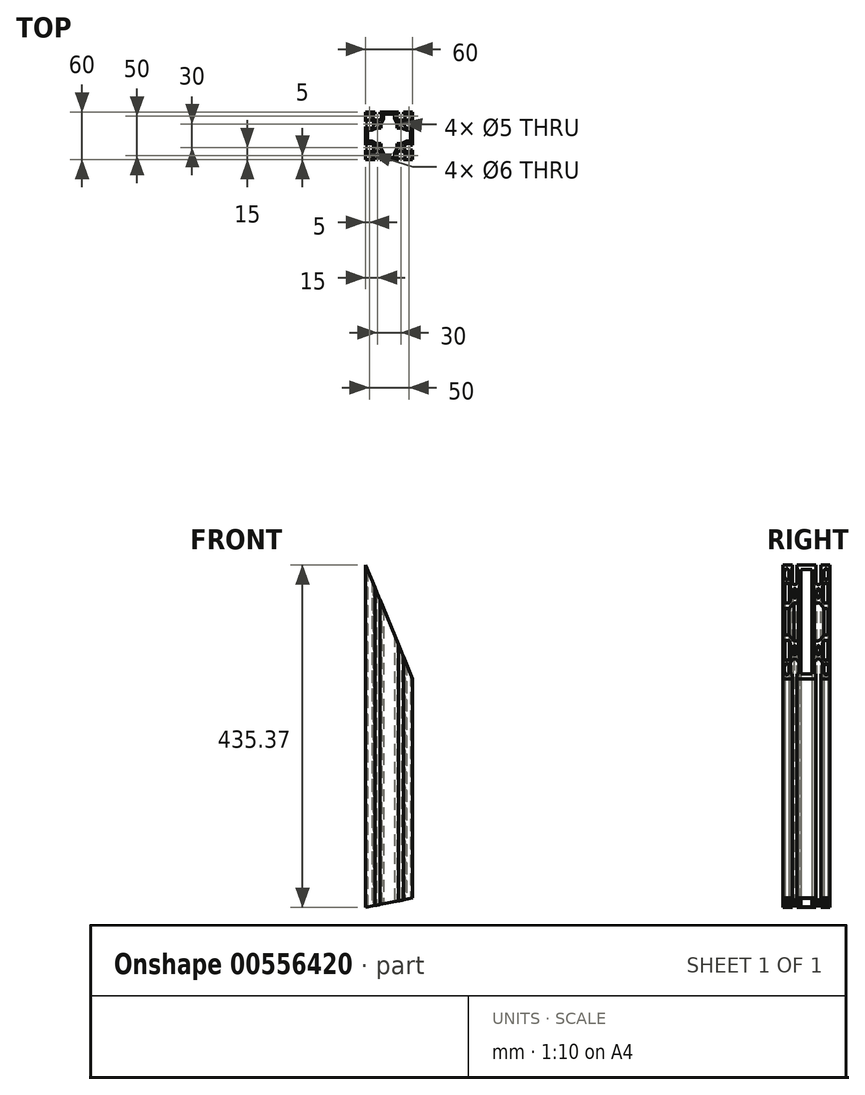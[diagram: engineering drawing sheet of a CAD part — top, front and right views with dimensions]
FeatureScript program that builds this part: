
annotation { "Feature Type Name" : "Feature", "Feature Type Description" : "" }
export const myFeature = defineFeature(function(context is Context, id is Id, definition is map)
    precondition{}
    {
        {
            var Q0;
            Q0=qCreatedBy(makeId("Top.planeOp"),FACE);
            var sketch = newSketch(context, id + "F0", { "sketchPlane" : qUnion([Q0])});
            skLineSegment(sketch, "E0.bottom", {"start": v(30, -30) * mm, "end": v(-30, -30) * mm});
            skLineSegment(sketch, "E0.top", {"start": v(30, 30) * mm, "end": v(-30, 30) * mm});
            skLineSegment(sketch, "E0.left", {"start": v(30, -30) * mm, "end": v(30, 30) * mm});
            skLineSegment(sketch, "E0.right", {"start": v(-30, -30) * mm, "end": v(-30, 30) * mm});
            skPoint(sketch, "E0.middle", {"position": v(0, 0) * mm});
            skLineSegment(sketch, "E1.top", {"start": v(-11.85, 30) * mm, "end": v(-18.15, 30) * mm});
            skLineSegment(sketch, "E1.left", {"start": v(-11.85, 27.5) * mm, "end": v(-11.85, 30) * mm});
            skLineSegment(sketch, "E1.right", {"start": v(-18.15, 27.5) * mm, "end": v(-18.15, 30) * mm});
            skPoint(sketch, "E1.middle", {"position": v(-15, 28.75) * mm});
            skLineSegment(sketch, "E2.bottom", {"start": v(-9.85, 27.5) * mm, "end": v(-11.85, 27.5) * mm});
            skLineSegment(sketch, "E2.left", {"start": v(-9.85, 27.5) * mm, "end": v(-9.85, 21.55) * mm});
            skLineSegment(sketch, "E2.right", {"start": v(-20.15, 27.5) * mm, "end": v(-20.15, 21.55) * mm});
            skPoint(sketch, "E2.middle", {"position": v(-15, 24.52) * mm});
            skArc(sketch, "E3", {"start": v(-20.15, 21.55) * mm, "mid": v(-15, 19.5) * mm, "end": v(-9.85, 21.55) * mm});
            skPoint(sketch, "E4.MirrorP", {"position": v(15, 24.52) * mm});
            skPoint(sketch, "E5.MirrorP", {"position": v(15, 28.75) * mm});
            skLineSegment(sketch, "E6.MirrorCS", {"start": v(11.85, 27.5) * mm, "end": v(11.85, 30) * mm});
            skLineSegment(sketch, "E7.MirrorCS", {"start": v(18.15, 27.5) * mm, "end": v(18.15, 30) * mm});
            skLineSegment(sketch, "E8.MirrorCS", {"start": v(9.85, 27.5) * mm, "end": v(11.85, 27.5) * mm});
            skLineSegment(sketch, "E9.MirrorCS", {"start": v(9.85, 27.5) * mm, "end": v(9.85, 21.55) * mm});
            skArc(sketch, "E10.MirrorCS", {"start": v(20.15, 21.55) * mm, "mid": v(15, 19.5) * mm, "end": v(9.85, 21.55) * mm});
            skLineSegment(sketch, "E11.MirrorCS", {"start": v(20.15, 27.5) * mm, "end": v(20.15, 21.55) * mm});
            skLineSegment(sketch, "E12.MirrorCS", {"start": v(11.85, 30) * mm, "end": v(18.15, 30) * mm});
            skLineSegment(sketch, "E13.1.0", {"start": v(27.5, 20.15) * mm, "end": v(21.55, 20.15) * mm});
            skLineSegment(sketch, "E13.1.1", {"start": v(27.5, 9.85) * mm, "end": v(21.55, 9.85) * mm});
            skArc(sketch, "E13.1.2", {"start": v(21.55, 20.15) * mm, "mid": v(19.5, 15) * mm, "end": v(21.55, 9.85) * mm});
            skLineSegment(sketch, "E13.1.3", {"start": v(27.5, -9.85) * mm, "end": v(21.55, -9.85) * mm});
            skLineSegment(sketch, "E13.1.4", {"start": v(27.5, -20.15) * mm, "end": v(21.55, -20.15) * mm});
            skPoint(sketch, "E13.1.5", {"position": v(28.75, 15) * mm});
            skPoint(sketch, "E13.1.6", {"position": v(28.75, -15) * mm});
            skArc(sketch, "E13.1.7", {"start": v(21.55, -20.15) * mm, "mid": v(19.5, -15) * mm, "end": v(21.55, -9.85) * mm});
            skPoint(sketch, "E13.1.8", {"position": v(24.52, -15) * mm});
            skPoint(sketch, "E13.1.9", {"position": v(24.52, 15) * mm});
            skLineSegment(sketch, "E13.1.10", {"start": v(27.5, 9.85) * mm, "end": v(27.5, 20.15) * mm});
            skLineSegment(sketch, "E13.1.11", {"start": v(27.5, -11.85) * mm, "end": v(27.5, -18.15) * mm});
            skLineSegment(sketch, "E13.1.12", {"start": v(30, 11.85) * mm, "end": v(30, 18.15) * mm});
            skLineSegment(sketch, "E13.1.13", {"start": v(30, -11.85) * mm, "end": v(30, -18.15) * mm});
            skLineSegment(sketch, "E13.1.14", {"start": v(27.5, 18.15) * mm, "end": v(30, 18.15) * mm});
            skLineSegment(sketch, "E13.1.15", {"start": v(27.5, 11.85) * mm, "end": v(30, 11.85) * mm});
            skLineSegment(sketch, "E13.1.16", {"start": v(27.5, 11.85) * mm, "end": v(27.5, 18.15) * mm});
            skLineSegment(sketch, "E13.1.17", {"start": v(27.5, -9.85) * mm, "end": v(27.5, -20.15) * mm});
            skLineSegment(sketch, "E13.1.18", {"start": v(27.5, -18.15) * mm, "end": v(30, -18.15) * mm});
            skLineSegment(sketch, "E13.1.19", {"start": v(27.5, -11.85) * mm, "end": v(30, -11.85) * mm});
            skLineSegment(sketch, "E13.2.0", {"start": v(20.15, -27.5) * mm, "end": v(20.15, -21.55) * mm});
            skLineSegment(sketch, "E13.2.1", {"start": v(9.85, -27.5) * mm, "end": v(9.85, -21.55) * mm});
            skArc(sketch, "E13.2.2", {"start": v(20.15, -21.55) * mm, "mid": v(15, -19.5) * mm, "end": v(9.85, -21.55) * mm});
            skLineSegment(sketch, "E13.2.3", {"start": v(-9.85, -27.5) * mm, "end": v(-9.85, -21.55) * mm});
            skLineSegment(sketch, "E13.2.4", {"start": v(-20.15, -27.5) * mm, "end": v(-20.15, -21.55) * mm});
            skPoint(sketch, "E13.2.5", {"position": v(15, -28.75) * mm});
            skPoint(sketch, "E13.2.6", {"position": v(-15, -28.75) * mm});
            skArc(sketch, "E13.2.7", {"start": v(-20.15, -21.55) * mm, "mid": v(-15, -19.5) * mm, "end": v(-9.85, -21.55) * mm});
            skPoint(sketch, "E13.2.8", {"position": v(-15, -24.52) * mm});
            skPoint(sketch, "E13.2.9", {"position": v(15, -24.52) * mm});
            skLineSegment(sketch, "E13.2.10", {"start": v(9.85, -27.5) * mm, "end": v(20.15, -27.5) * mm});
            skLineSegment(sketch, "E13.2.11", {"start": v(-11.85, -27.5) * mm, "end": v(-18.15, -27.5) * mm});
            skLineSegment(sketch, "E13.2.12", {"start": v(11.85, -30) * mm, "end": v(18.15, -30) * mm});
            skLineSegment(sketch, "E13.2.13", {"start": v(-11.85, -30) * mm, "end": v(-18.15, -30) * mm});
            skLineSegment(sketch, "E13.2.14", {"start": v(18.15, -27.5) * mm, "end": v(18.15, -30) * mm});
            skLineSegment(sketch, "E13.2.15", {"start": v(11.85, -27.5) * mm, "end": v(11.85, -30) * mm});
            skLineSegment(sketch, "E13.2.16", {"start": v(11.85, -27.5) * mm, "end": v(18.15, -27.5) * mm});
            skLineSegment(sketch, "E13.2.17", {"start": v(-9.85, -27.5) * mm, "end": v(-20.15, -27.5) * mm});
            skLineSegment(sketch, "E13.2.18", {"start": v(-18.15, -27.5) * mm, "end": v(-18.15, -30) * mm});
            skLineSegment(sketch, "E13.2.19", {"start": v(-11.85, -27.5) * mm, "end": v(-11.85, -30) * mm});
            skLineSegment(sketch, "E13.3.0", {"start": v(-27.5, -20.15) * mm, "end": v(-21.55, -20.15) * mm});
            skLineSegment(sketch, "E13.3.1", {"start": v(-27.5, -9.85) * mm, "end": v(-21.55, -9.85) * mm});
            skArc(sketch, "E13.3.2", {"start": v(-21.55, -20.15) * mm, "mid": v(-19.5, -15) * mm, "end": v(-21.55, -9.85) * mm});
            skLineSegment(sketch, "E13.3.3", {"start": v(-27.5, 9.85) * mm, "end": v(-21.55, 9.85) * mm});
            skLineSegment(sketch, "E13.3.4", {"start": v(-27.5, 20.15) * mm, "end": v(-21.55, 20.15) * mm});
            skPoint(sketch, "E13.3.5", {"position": v(-28.75, -15) * mm});
            skPoint(sketch, "E13.3.6", {"position": v(-28.75, 15) * mm});
            skArc(sketch, "E13.3.7", {"start": v(-21.55, 20.15) * mm, "mid": v(-19.5, 15) * mm, "end": v(-21.55, 9.85) * mm});
            skPoint(sketch, "E13.3.8", {"position": v(-24.52, 15) * mm});
            skPoint(sketch, "E13.3.9", {"position": v(-24.52, -15) * mm});
            skLineSegment(sketch, "E13.3.10", {"start": v(-27.5, -9.85) * mm, "end": v(-27.5, -20.15) * mm});
            skLineSegment(sketch, "E13.3.11", {"start": v(-27.5, 11.85) * mm, "end": v(-27.5, 18.15) * mm});
            skLineSegment(sketch, "E13.3.12", {"start": v(-30, -11.85) * mm, "end": v(-30, -18.15) * mm});
            skLineSegment(sketch, "E13.3.13", {"start": v(-30, 11.85) * mm, "end": v(-30, 18.15) * mm});
            skLineSegment(sketch, "E13.3.14", {"start": v(-27.5, -18.15) * mm, "end": v(-30, -18.15) * mm});
            skLineSegment(sketch, "E13.3.15", {"start": v(-27.5, -11.85) * mm, "end": v(-30, -11.85) * mm});
            skLineSegment(sketch, "E13.3.16", {"start": v(-27.5, -11.85) * mm, "end": v(-27.5, -18.15) * mm});
            skLineSegment(sketch, "E13.3.17", {"start": v(-27.5, 9.85) * mm, "end": v(-27.5, 20.15) * mm});
            skLineSegment(sketch, "E13.3.18", {"start": v(-27.5, 18.15) * mm, "end": v(-30, 18.15) * mm});
            skLineSegment(sketch, "E13.3.19", {"start": v(-27.5, 11.85) * mm, "end": v(-30, 11.85) * mm});
            skLineSegment(sketch, "E13.anchor1", {"start": v(0, 0) * mm, "end": v(-20.15, 21.55) * mm, "construction": true});
            skLineSegment(sketch, "E13.anchor2", {"start": v(0, 0) * mm, "end": v(-21.55, -20.15) * mm, "construction": true});
            skLineSegment(sketch, "E14.trimOffspring", {"start": v(-18.15, 27.5) * mm, "end": v(-20.15, 27.5) * mm});
            skLineSegment(sketch, "E15.trimOffspring", {"start": v(18.15, 27.5) * mm, "end": v(20.15, 27.5) * mm});
            skCircle(sketch, "E16", {"center": v(-15, 15) * mm, "radius": 2.5 * mm});
            skCircle(sketch, "E17", {"center": v(-25, 25) * mm, "radius": 3 * mm});
            skCircle(sketch, "E18.MirrorC", {"center": v(25, 25) * mm, "radius": 3 * mm});
            skCircle(sketch, "E19.MirrorC", {"center": v(25, -25) * mm, "radius": 3 * mm});
            skCircle(sketch, "E20.MirrorC", {"center": v(-25, -25) * mm, "radius": 3 * mm});
            skCircle(sketch, "E21.MirrorC", {"center": v(15, 15) * mm, "radius": 2.5 * mm});
            skCircle(sketch, "E22.MirrorC", {"center": v(15, -15) * mm, "radius": 2.5 * mm});
            skCircle(sketch, "E23.MirrorC", {"center": v(-15, -15) * mm, "radius": 2.5 * mm});
            skLineSegment(sketch, "E24", {"start": v(-7, 27.5) * mm, "end": v(0, 27.5) * mm});
            skLineSegment(sketch, "E25", {"start": v(-7, 27.5) * mm, "end": v(-7, 22) * mm});
            skLineSegment(sketch, "E26", {"start": v(-10, 10) * mm, "end": v(-10, 16) * mm});
            skLineSegment(sketch, "E27", {"start": v(-10, 16) * mm, "end": v(-7, 22) * mm});
            skLineSegment(sketch, "E28.MirrorCS", {"start": v(10, 10) * mm, "end": v(10, 16) * mm});
            skLineSegment(sketch, "E29.MirrorCS", {"start": v(10, 16) * mm, "end": v(7, 22) * mm});
            skLineSegment(sketch, "E30.MirrorCS", {"start": v(7, 27.5) * mm, "end": v(0, 27.5) * mm});
            skLineSegment(sketch, "E31.MirrorCS", {"start": v(7, 27.5) * mm, "end": v(7, 22) * mm});
            skLineSegment(sketch, "E32.1.0", {"start": v(-10, -10) * mm, "end": v(-16, -10) * mm});
            skLineSegment(sketch, "E32.1.1", {"start": v(-16, -10) * mm, "end": v(-22, -7) * mm});
            skLineSegment(sketch, "E32.1.2", {"start": v(-27.5, -7) * mm, "end": v(-22, -7) * mm});
            skLineSegment(sketch, "E32.1.3", {"start": v(-27.5, -7) * mm, "end": v(-27.5, 0) * mm});
            skLineSegment(sketch, "E32.1.4", {"start": v(-27.5, 7) * mm, "end": v(-27.5, 0) * mm});
            skLineSegment(sketch, "E32.1.5", {"start": v(-27.5, 7) * mm, "end": v(-22, 7) * mm});
            skLineSegment(sketch, "E32.1.6", {"start": v(-16, 10) * mm, "end": v(-22, 7) * mm});
            skLineSegment(sketch, "E32.1.7", {"start": v(-10, 10) * mm, "end": v(-16, 10) * mm});
            skLineSegment(sketch, "E32.2.0", {"start": v(10, -10) * mm, "end": v(10, -16) * mm});
            skLineSegment(sketch, "E32.2.1", {"start": v(10, -16) * mm, "end": v(7, -22) * mm});
            skLineSegment(sketch, "E32.2.2", {"start": v(7, -27.5) * mm, "end": v(7, -22) * mm});
            skLineSegment(sketch, "E32.2.3", {"start": v(7, -27.5) * mm, "end": v(0, -27.5) * mm});
            skLineSegment(sketch, "E32.2.4", {"start": v(-7, -27.5) * mm, "end": v(0, -27.5) * mm});
            skLineSegment(sketch, "E32.2.5", {"start": v(-7, -27.5) * mm, "end": v(-7, -22) * mm});
            skLineSegment(sketch, "E32.2.6", {"start": v(-10, -16) * mm, "end": v(-7, -22) * mm});
            skLineSegment(sketch, "E32.2.7", {"start": v(-10, -10) * mm, "end": v(-10, -16) * mm});
            skLineSegment(sketch, "E32.3.0", {"start": v(10, 10) * mm, "end": v(16, 10) * mm});
            skLineSegment(sketch, "E32.3.1", {"start": v(16, 10) * mm, "end": v(22, 7) * mm});
            skLineSegment(sketch, "E32.3.2", {"start": v(27.5, 7) * mm, "end": v(22, 7) * mm});
            skLineSegment(sketch, "E32.3.3", {"start": v(27.5, 7) * mm, "end": v(27.5, 0) * mm});
            skLineSegment(sketch, "E32.3.4", {"start": v(27.5, -7) * mm, "end": v(27.5, 0) * mm});
            skLineSegment(sketch, "E32.3.5", {"start": v(27.5, -7) * mm, "end": v(22, -7) * mm});
            skLineSegment(sketch, "E32.3.6", {"start": v(16, -10) * mm, "end": v(22, -7) * mm});
            skLineSegment(sketch, "E32.3.7", {"start": v(10, -10) * mm, "end": v(16, -10) * mm});
            skSolve(sketch);
        }
        {
            var Q0;
            {var subQ30=sQuery(id+"F0.wireOp",EDGE,"E1.left");Q0=makeQuery(id+"F0.imprint","IMPRINT",FACE,{"disambiguationData":[TD([[makeQuery(id+"F0.imprint","IMPRINT",EDGE,{"derivedFrom":subQ30}),-1.0]])]});}
            extrude(context, id + "F1", {"entities" : qUnion([Q0]), "depth" : 435.37 * mm, "offsetDistance" : 25 * mm});
        }
        {
            var Q0;
            Q0=makeQuery(id+"F1.opExtrude","SWEPT_EDGE",EDGE,{"disambiguationData":[OSD([sQuery(id+"F0.wireOp",EDGE,"E24"),sQuery(id+"F0.wireOp",EDGE,"E25")])]});
            var Q1;
            Q1=makeQuery(id+"F1.opExtrude","SWEPT_EDGE",EDGE,{"disambiguationData":[OSD([sQuery(id+"F0.wireOp",EDGE,"E30.MirrorCS"),sQuery(id+"F0.wireOp",EDGE,"E31.MirrorCS")])]});
            var Q2;
            Q2=makeQuery(id+"F1.opExtrude","SWEPT_EDGE",EDGE,{"disambiguationData":[OSD([sQuery(id+"F0.wireOp",EDGE,"840db5bc-c403-45cd-90c7-254e62d9e8c5.3.2"),sQuery(id+"F0.wireOp",EDGE,"840db5bc-c403-45cd-90c7-254e62d9e8c5.3.3")])]});
            var Q3;
            Q3=makeQuery(id+"F1.opExtrude","SWEPT_EDGE",EDGE,{"disambiguationData":[OSD([sQuery(id+"F0.wireOp",EDGE,"840db5bc-c403-45cd-90c7-254e62d9e8c5.3.4"),sQuery(id+"F0.wireOp",EDGE,"840db5bc-c403-45cd-90c7-254e62d9e8c5.3.5")])]});
            var Q4;
            Q4=makeQuery(id+"F1.opExtrude","SWEPT_EDGE",EDGE,{"disambiguationData":[OSD([sQuery(id+"F0.wireOp",EDGE,"840db5bc-c403-45cd-90c7-254e62d9e8c5.1.4"),sQuery(id+"F0.wireOp",EDGE,"840db5bc-c403-45cd-90c7-254e62d9e8c5.1.5")])]});
            var Q5;
            Q5=makeQuery(id+"F1.opExtrude","SWEPT_EDGE",EDGE,{"disambiguationData":[OSD([sQuery(id+"F0.wireOp",EDGE,"840db5bc-c403-45cd-90c7-254e62d9e8c5.1.2"),sQuery(id+"F0.wireOp",EDGE,"840db5bc-c403-45cd-90c7-254e62d9e8c5.1.3")])]});
            var Q6;
            Q6=makeQuery(id+"F1.opExtrude","SWEPT_EDGE",EDGE,{"disambiguationData":[OSD([sQuery(id+"F0.wireOp",EDGE,"840db5bc-c403-45cd-90c7-254e62d9e8c5.2.2"),sQuery(id+"F0.wireOp",EDGE,"840db5bc-c403-45cd-90c7-254e62d9e8c5.2.3")])]});
            var Q7;
            Q7=makeQuery(id+"F1.opExtrude","SWEPT_EDGE",EDGE,{"disambiguationData":[OSD([sQuery(id+"F0.wireOp",EDGE,"840db5bc-c403-45cd-90c7-254e62d9e8c5.2.4"),sQuery(id+"F0.wireOp",EDGE,"840db5bc-c403-45cd-90c7-254e62d9e8c5.2.5")])]});
            fillet(context, id + "F2", {"entities" : qUnion([Q0, Q1, Q2, Q3, Q4, Q5, Q6, Q7]), "radius" : 2 * mm, "tangentPropagation" : true, "allowEdgeOverflow" : false});
        }
        {
            var Q0;
            Q0=makeQuery(id+"F1.opExtrude","SWEPT_EDGE",EDGE,{"disambiguationData":[OSD([sQuery(id+"F0.wireOp",EDGE,"E26"),sQuery(id+"F0.wireOp",EDGE,"E27")])]});
            var Q1;
            Q1=makeQuery(id+"F1.opExtrude","SWEPT_EDGE",EDGE,{"disambiguationData":[OSD([sQuery(id+"F0.wireOp",EDGE,"E28.MirrorCS"),sQuery(id+"F0.wireOp",EDGE,"E29.MirrorCS")])]});
            var Q2;
            Q2=makeQuery(id+"F1.opExtrude","SWEPT_EDGE",EDGE,{"disambiguationData":[OSD([sQuery(id+"F0.wireOp",EDGE,"840db5bc-c403-45cd-90c7-254e62d9e8c5.3.0"),sQuery(id+"F0.wireOp",EDGE,"840db5bc-c403-45cd-90c7-254e62d9e8c5.3.1")])]});
            var Q3;
            Q3=makeQuery(id+"F1.opExtrude","SWEPT_EDGE",EDGE,{"disambiguationData":[OSD([sQuery(id+"F0.wireOp",EDGE,"840db5bc-c403-45cd-90c7-254e62d9e8c5.1.6"),sQuery(id+"F0.wireOp",EDGE,"840db5bc-c403-45cd-90c7-254e62d9e8c5.1.7")])]});
            var Q4;
            Q4=makeQuery(id+"F1.opExtrude","SWEPT_EDGE",EDGE,{"disambiguationData":[OSD([sQuery(id+"F0.wireOp",EDGE,"840db5bc-c403-45cd-90c7-254e62d9e8c5.1.0"),sQuery(id+"F0.wireOp",EDGE,"840db5bc-c403-45cd-90c7-254e62d9e8c5.1.1")])]});
            var Q5;
            Q5=makeQuery(id+"F1.opExtrude","SWEPT_EDGE",EDGE,{"disambiguationData":[OSD([sQuery(id+"F0.wireOp",EDGE,"840db5bc-c403-45cd-90c7-254e62d9e8c5.3.6"),sQuery(id+"F0.wireOp",EDGE,"840db5bc-c403-45cd-90c7-254e62d9e8c5.3.7")])]});
            var Q6;
            Q6=makeQuery(id+"F1.opExtrude","SWEPT_EDGE",EDGE,{"disambiguationData":[OSD([sQuery(id+"F0.wireOp",EDGE,"840db5bc-c403-45cd-90c7-254e62d9e8c5.2.0"),sQuery(id+"F0.wireOp",EDGE,"840db5bc-c403-45cd-90c7-254e62d9e8c5.2.1")])]});
            var Q7;
            Q7=makeQuery(id+"F1.opExtrude","SWEPT_EDGE",EDGE,{"disambiguationData":[OSD([sQuery(id+"F0.wireOp",EDGE,"840db5bc-c403-45cd-90c7-254e62d9e8c5.2.6"),sQuery(id+"F0.wireOp",EDGE,"840db5bc-c403-45cd-90c7-254e62d9e8c5.2.7")])]});
            fillet(context, id + "F3", {"entities" : qUnion([Q0, Q1, Q2, Q3, Q4, Q5, Q6, Q7]), "radius" : 7 * mm, "tangentPropagation" : true, "allowEdgeOverflow" : false});
        }
        {
            var Q0;
            Q0=qCreatedBy(makeId("Front.planeOp"),FACE);
            var sketch = newSketch(context, id + "F4", { "sketchPlane" : qUnion([Q0])});
            skLineSegment(sketch, "E33.bottom", {"start": v(176.13, -193.02) * mm, "end": v(131.35, 32.1) * mm});
            skLineSegment(sketch, "E33.top", {"start": v(14.78, -225.12) * mm, "end": v(-30, 0) * mm});
            skLineSegment(sketch, "E33.left", {"start": v(176.13, -193.02) * mm, "end": v(14.78, -225.12) * mm});
            skLineSegment(sketch, "E33.right", {"start": v(131.35, 32.1) * mm, "end": v(-30, 0) * mm});
            skLineSegment(sketch, "E34.bottom", {"start": v(-30, 435.37) * mm, "end": v(207.06, 533.56) * mm});
            skLineSegment(sketch, "E34.top", {"start": v(64.67, 206.82) * mm, "end": v(301.73, 305.01) * mm});
            skLineSegment(sketch, "E34.left", {"start": v(-30, 435.37) * mm, "end": v(64.67, 206.82) * mm});
            skLineSegment(sketch, "E34.right", {"start": v(207.06, 533.56) * mm, "end": v(301.73, 305.01) * mm});
            skSolve(sketch);
        }
        {
            var Q0;
            Q0=qSketchRegion(id+"F4",true);
            extrude(context, id + "F5", {"entities" : qUnion([Q0]), "operationType" : NewBodyOperationType.REMOVE, "depth" : 30 * mm, "offsetDistance" : 25 * mm, "hasSecondDirection" : true, "secondDirectionOppositeDirection" : true, "secondDirectionDepth" : 30 * mm});
        }
    });
